# Revit family: SL75_H_MAY22
name_source: partatom
category: Mechanical Equipment
units: mm (PartAtom-declared; Revit-internal decimal feet)

## family parameters
Always vertical = Yes
Cut with Voids When Loaded = No
Part Type = Normal
Room Calculation Point = No
Round Connector Dimension = Use Diameter
Shared = No
Work Plane-Based = No

## types (1)
- SL75_H_MAY22
    Accessories = Backdraft damper 6", Wall cap 6" - white, brown, Digital time clock - wall mount (TC7D-W), in exterior enclosure (TC7D-E), Carbon dioxide sensor/control - wall mount (CO2-W), IAQ sensor - wall mount (IAQ-W), Motion occupancy sensor/control - ceiling mount (MC-C), wall mount (MC-W), Percentage timer control (PTL), Percentage timer control with furnace interlock (FM), Push-button point-of-use controls (PBL), PTL req'd., MERV 13 Filter - OA airstream, Wall bracket kit, Electric duct heater - RH series (1-4 kW); designed for indoor ductwork installation only
    Continuous Operation Airflow = 30-130 CFM
    Controls = Onboard digital controller with independent variable speeds
    Description = Energy Recovery Ventilator
    Energy Recovery Type = Static plate, heat and humidity transfer
    FLA per Motor = 2
    Filters = Total qty. 2, MERV 8, spun-polyester media: 7-1/2" x 10-1/2" x 1"
    Hertz = 60
    Manufacturer = Renewaire LLC
    Max. Shipping Dimensions (in carton) = 31 1/4" L x 22-3/8" W x 14-3/8" H
    Max. Shipping Weight (in carton) = 41 lbs.
    Maximum Overcurrent Protection = 15
    Minimum Circuit Amps = 10
    Model = SL70L
    Motor(s) = Qty. 2, 48V DC motorized impeller packages
    Phase = 1
    Service Area = Renewaire - Interference
    Service Area Visibility = Yes
    Standard Features = Unit may be mounted in any orientation, Low-voltage circuit for controls, Hard wiring in electrical box, Dial-A-Flow - balance and airflow adjustment, Variable speed, Boost mode, Cross-core differential pressure ports, Gray painted cabinet
    URL = www.renewaire.com
    Unit Dimensions = 30-3/4" L x 20-3/8" W x 9-1/2" H
    Unit Weight = 35 lbs.
    Voltage = 120
    Watts = 53

## geometry (parser evidence)
native form markers: Sweep x2
no freeform markers — native parametric forms only
